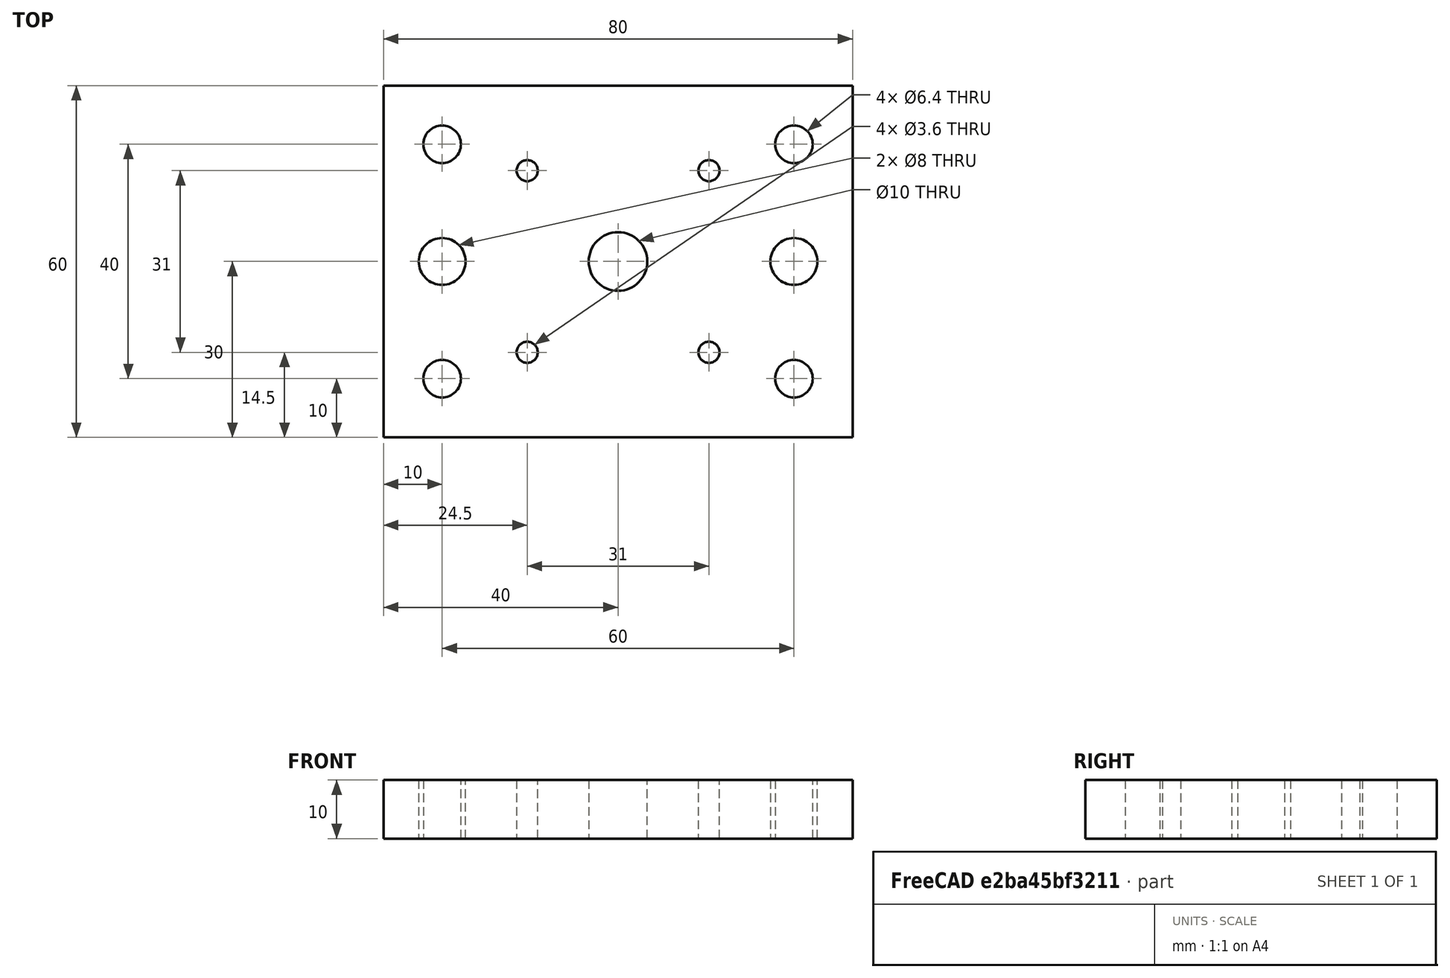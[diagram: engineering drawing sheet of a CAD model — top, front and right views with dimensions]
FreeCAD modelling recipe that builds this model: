
FCSTD DOCUMENT  (FreeCAD 0.18R16110 (Git))
Label: mountplate1c
License: All rights reserved
LicenseURL: http://en.wikipedia.org/wiki/All_rights_reserved
objects: Sketcher::SketchObject×1, PartDesign::Pad×1, PartDesign::Body×1
note: 4 computed .brp shape members not serialized (recipe doc carries the construction recipe); baked Part::Feature solids carry a one-line shape summary decoded from their .brp

FEATURE [Sketcher::SketchObject] Sketch
  MapMode = 5
  Support = -> [XY_Plane]
  sketch-geometry (15):
    g0: LineSegment StartX=0 StartY=60 StartZ=0 EndX=80 EndY=60 EndZ=0
    g1: LineSegment StartX=80 StartY=60 StartZ=0 EndX=80 EndY=0 EndZ=0
    g2: LineSegment StartX=80 StartY=0 StartZ=0 EndX=0 EndY=0 EndZ=0
    g3: LineSegment StartX=0 StartY=0 StartZ=0 EndX=0 EndY=60 EndZ=0
    g4: Circle CenterX=40 CenterY=30 CenterZ=0 NormalX=0 NormalY=0 NormalZ=1 AngleXU=0 Radius=5
    g5: Circle CenterX=55.5 CenterY=45.5 CenterZ=0 NormalX=0 NormalY=0 NormalZ=1 AngleXU=0 Radius=1.8
    g6: Circle CenterX=55.5 CenterY=14.5 CenterZ=0 NormalX=0 NormalY=0 NormalZ=1 AngleXU=0 Radius=1.8
    g7: Circle CenterX=24.5 CenterY=14.5 CenterZ=0 NormalX=0 NormalY=0 NormalZ=1 AngleXU=0 Radius=1.8
    g8: Circle CenterX=24.5 CenterY=45.5 CenterZ=0 NormalX=0 NormalY=0 NormalZ=1 AngleXU=0 Radius=1.8
    g9: Circle CenterX=10 CenterY=10 CenterZ=0 NormalX=0 NormalY=0 NormalZ=1 AngleXU=0 Radius=3.2
    g10: Circle CenterX=70 CenterY=10 CenterZ=0 NormalX=0 NormalY=0 NormalZ=1 AngleXU=0 Radius=3.2
    g11: Circle CenterX=70 CenterY=30 CenterZ=0 NormalX=0 NormalY=0 NormalZ=1 AngleXU=0 Radius=4
    g12: Circle CenterX=10 CenterY=30 CenterZ=0 NormalX=0 NormalY=0 NormalZ=1 AngleXU=0 Radius=4
    g13: Circle CenterX=10 CenterY=50 CenterZ=0 NormalX=0 NormalY=0 NormalZ=1 AngleXU=0 Radius=3.2
    g14: Circle CenterX=70 CenterY=50 CenterZ=0 NormalX=0 NormalY=0 NormalZ=1 AngleXU=0 Radius=3.2
  constraints (44):
    c: Coincident(g0,g1)
    c: Coincident(g1,g2)
    c: Coincident(g2,g3)
    c: Coincident(g3,g0)
    c: Horizontal(g0)
    c: Horizontal(g2)
    c: Vertical(g1)
    c: Vertical(g3)
    c: Coincident(g2,g-1)
    c: DistanceY(g3,g3) = 60
    c: DistanceX(g2,g2) = 80
    c: DistanceX(g2,g4) = 40
    c: DistanceY(g2,g4) = 30
    c: Radius(g4) = 5
    c: DistanceY(g4,g5) = 15.5
    c: DistanceX(g6,g5) = 0
    c: DistanceX(g4,g5) = 15.5
    c: DistanceY(g8,g5) = 0
    c: DistanceX(g8,g5) = 31
    c: DistanceX(g7,g8) = 0
    c: DistanceY(g6,g5) = 31
    c: DistanceY(g6,g7) = 0
    c: Radius(g8) = 1.8
    c: Equal(g8,g5)
    c: Equal(g8,g6)
    c: Equal(g8,g7)
    c: DistanceX(g2,g9) = 10
    c: DistanceY(g2,g9) = 10
    c: DistanceY(g9,g10) = 0
    c: DistanceX(g10,g1) = 10
    c: DistanceX(g12,g9) = 0
    c: DistanceY(g11,g12) = 0
    c: DistanceX(g11,g0) = 10
    c: DistanceY(g12,g0) = 30
    c: Radius(g9) = 3.2
    c: Equal(g9,g10)
    c: Radius(g12) = 4
    c: Equal(g12,g11)
    c: DistanceX(g11,g14) = 0
    c: DistanceX(g13,g12) = 0
    c: DistanceY(g13,g0) = 10
    c: DistanceY(g14,g0) = 10
    c: Radius(g14) = 3.2
    c: Radius(g13) = 3.2
FEATURE [PartDesign::Pad] Pad
  Length = 10
  Length2 = 100
  Profile = -> Sketch
  Type = 0
FEATURE [PartDesign::Body] Body
  Group = -> [Sketch,Pad]
  Origin = -> Origin
  Tip = -> Pad
